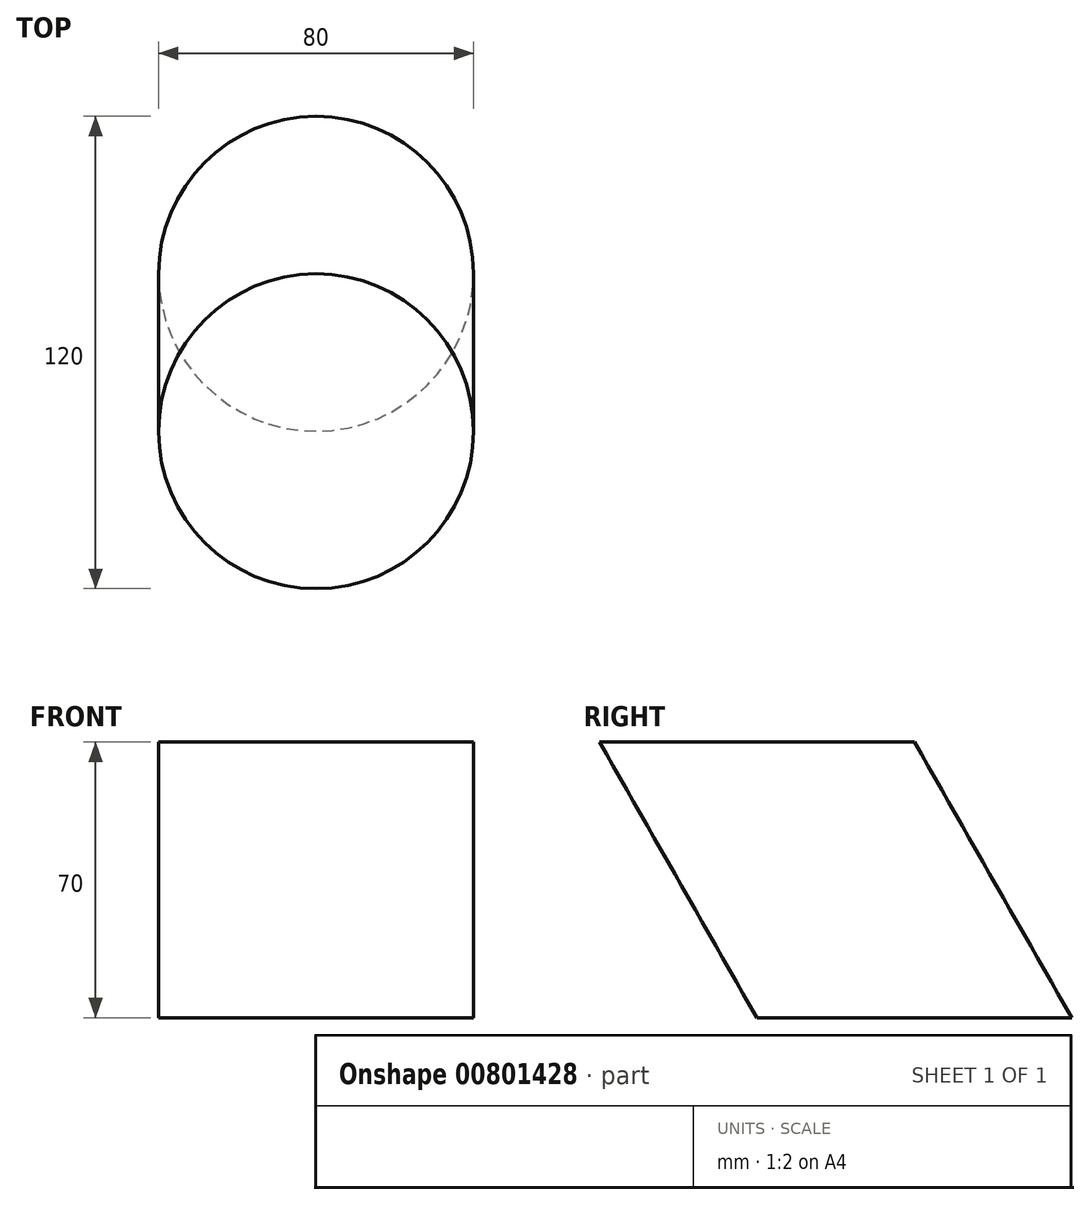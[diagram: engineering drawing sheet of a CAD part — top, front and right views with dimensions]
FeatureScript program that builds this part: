
annotation { "Feature Type Name" : "Feature", "Feature Type Description" : "" }
export const myFeature = defineFeature(function(context is Context, id is Id, definition is map)
    precondition{}
    {
        {
            var Q0;
            Q0=qCreatedBy(makeId("Top.planeOp"),FACE);
            var sketch = newSketch(context, id + "F0", { "sketchPlane" : qUnion([Q0])});
            skCircle(sketch, "E0", {"center": v(0, 0) * mm, "radius": 40 * mm});
            skSolve(sketch);
        }
        {
            var Q0;
            Q0=qCreatedBy(makeId("Top.planeOp"),FACE);
            cPlane(context, id + "F1", {"entities" : qUnion([Q0]), "cplaneType" : CPlaneType.OFFSET, "offset" : 70 * mm, "width" : 150 * mm, "height" : 150 * mm});
        }
        {
            var Q0;
            Q0=qCreatedBy(id+"F1.planeOp",FACE);
            var sketch = newSketch(context, id + "F2", { "sketchPlane" : qUnion([Q0])});
            skCircle(sketch, "E1", {"center": v(0, -40) * mm, "radius": 40 * mm});
            skSolve(sketch);
        }
        {
            var Q0;
            Q0=qCreatedBy(makeId("Right.planeOp"),FACE);
            var sketch = newSketch(context, id + "F3", { "sketchPlane" : qUnion([Q0])});
            skPoint(sketch, "E2.0", {"position": v(-40, 70) * mm});
            skPoint(sketch, "E3.0", {"position": v(0, 0) * mm});
            skLineSegment(sketch, "E4", {"start": v(0, 0) * mm, "end": v(-40, 70) * mm});
            skSolve(sketch);
        }
        {
            var Q0;
            Q0=makeQuery(id+"F0.imprint","IMPRINT",FACE,{"disambiguationData":[TD([[makeQuery(id+"F0.imprint","IMPRINT",EDGE,{"derivedFrom":sQuery(id+"F0.wireOp",EDGE,"E0")}),1.0]])]});
            var Q1;
            Q1=sQuery(id+"F3.wireOp",EDGE,"E4");
            sweep(context, id + "F4", {"profiles" : qUnion([Q0]), "path" : qUnion([Q1])});
        }
    });
